# Revit family: Gira_102400
name_source: partatom
category: Electrical Fixtures
revit_build: Autodesk Revit 2017 (Build: 20160225_1515(x64)
units: mm (PartAtom-declared; Revit-internal decimal feet)

## family parameters
Cut with Voids When Loaded = No
Host = Face
Maintain Annotation Orientation = No
Part Type = Normal
Room Calculation Point = No
Round Connector Dimension = Use Diameter
Shared = No

## types (1)
- Pow.supply AC 24 V 1 A DRA Accessories
    BIM = https://media.live.bim.site 8f.rfa
    BIMSITE_PRODUCT_ID = fb6a88596a59b92168ed2fe0f08236503b4a0cc7
    Bus connection included = No
    Cost = 0 $
    Default Elevation = 1219 mm
    Description = PS AC 24V 1A DRA Accs. Power supply AC 24 V 1 A,DRA Features: - Power supply for the weather station and the in-built heating of the wind sensor 0 - 10 V, rain sensor 0   10 V, etc.
    GTIN = 4010337010715
    HAN = 102400
    HeinzeBIM = https://www.heinze.de
    Local operation/hand operation = No
    Manufacturer = Gira
    Number of binary inputs = 0
    Number of outputs = 0
    Suitable for C-load = No
    URL = https://www.gira.de

## geometry (parser evidence)
native form markers: Blend x2, Sweep x3
no freeform markers — native parametric forms only
